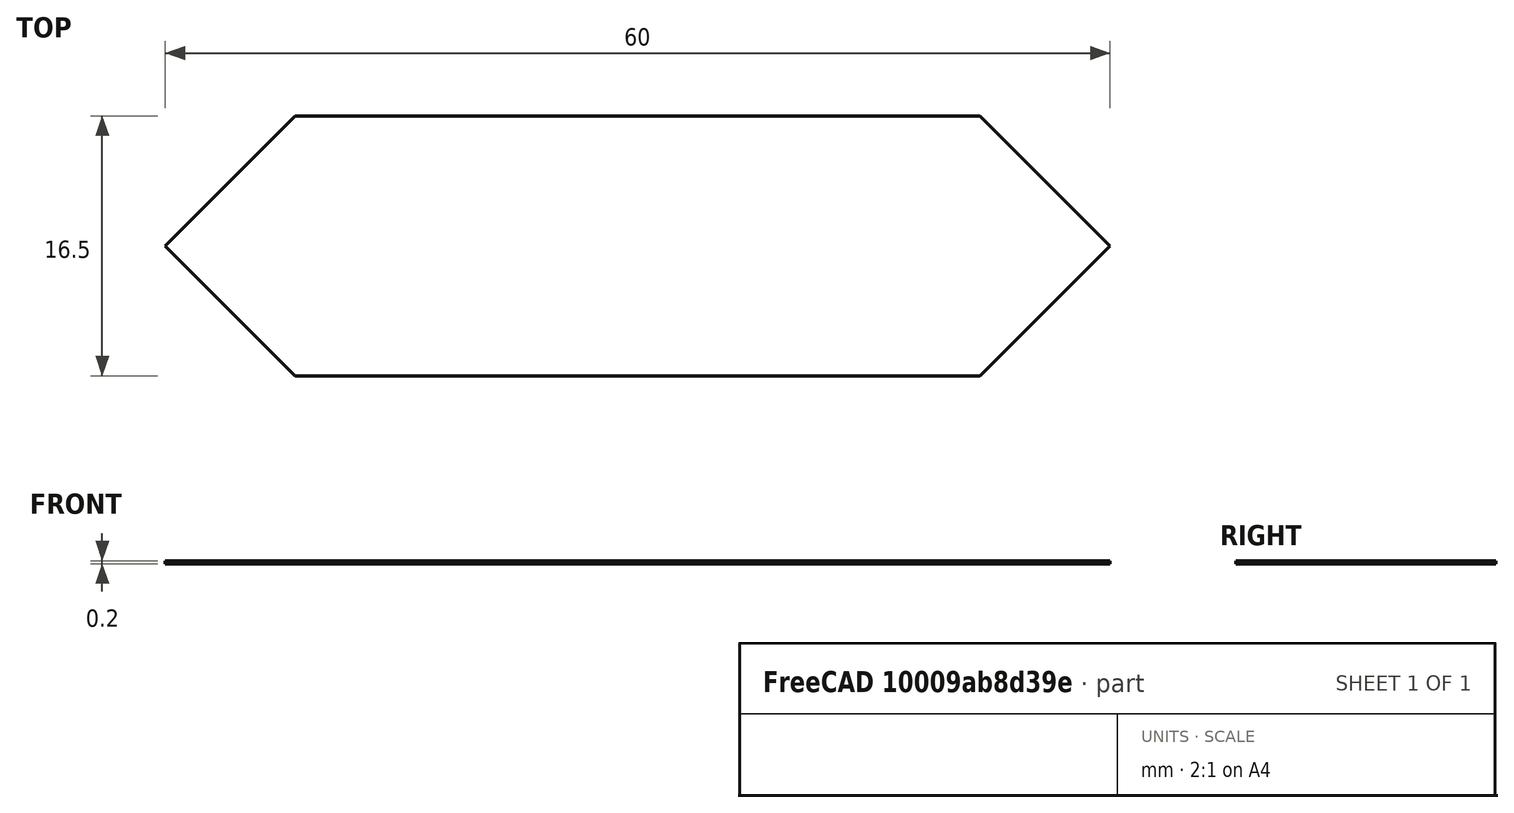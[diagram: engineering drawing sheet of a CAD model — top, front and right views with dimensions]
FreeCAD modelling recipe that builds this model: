
FCSTD DOCUMENT  (FreeCAD 0.20R29603 (Git))
Label: FacePlate_6016
License: All rights reserved
LicenseURL: http://en.wikipedia.org/wiki/All_rights_reserved
objects: Sketcher::SketchObject×1, PartDesign::Pad×1, PartDesign::Body×1
note: 4 computed .brp shape members not serialized (recipe doc carries the construction recipe); baked Part::Feature solids carry a one-line shape summary decoded from their .brp

FEATURE [Sketcher::SketchObject] Sketch
  FullyConstrained = true
  MapMode = 5
  Support = -> [XY_Plane]
  sketch-geometry (6):
    g0: LineSegment StartX=-21.75 StartY=8.25 StartZ=0 EndX=21.75 EndY=8.25 EndZ=0
    g1: LineSegment StartX=-21.75 StartY=-8.25 StartZ=0 EndX=21.75 EndY=-8.25 EndZ=0
    g2: LineSegment StartX=21.75 StartY=8.25 StartZ=0 EndX=30 EndY=0 EndZ=0
    g3: LineSegment StartX=21.75 StartY=-8.25 StartZ=0 EndX=30 EndY=0 EndZ=0
    g4: LineSegment StartX=-21.75 StartY=-8.25 StartZ=0 EndX=-30 EndY=0 EndZ=0
    g5: LineSegment StartX=-21.75 StartY=8.25 StartZ=0 EndX=-30 EndY=0 EndZ=0
  constraints (16):
    c: Horizontal(g0)
    c: Horizontal(g1)
    c: Coincident(g2,g0)
    c: PointOnObject(g2,g-1)
    c: Coincident(g3,g1)
    c: Coincident(g3,g2)
    c: Coincident(g4,g1)
    c: Coincident(g5,g0)
    c: Coincident(g5,g4)
    c: Angle(g4,g5) = 1.5708
    c: DistanceY(g1,g0) = 16.5
    c: Angle(g2,g3) = 1.5708
    c: Symmetric(g0,g1,g-1)
    c: Equal(g0,g1)
    c: Symmetric(g4,g2,g-2)
    c: DistanceX(g4,g2) = 60
FEATURE [PartDesign::Pad] Pad  label="Face"
  Direction = (0,0,1)
  Length = 0.2
  Length2 = 100
  Profile = -> Sketch
  Type = 0
FEATURE [PartDesign::Body] Body
  Group = -> [Sketch,Pad]
  Origin = -> Origin
  Tip = -> Pad
